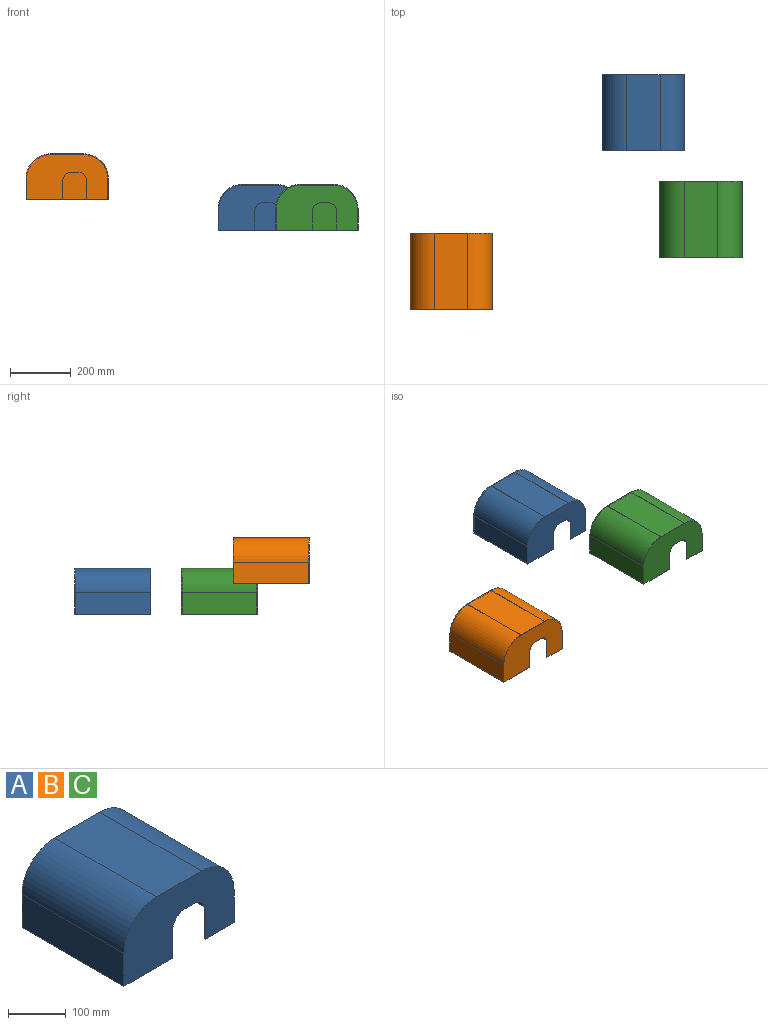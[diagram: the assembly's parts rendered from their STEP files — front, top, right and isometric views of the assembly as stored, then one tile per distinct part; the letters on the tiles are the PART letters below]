
ASSEMBLY  parts=3 mates=2
PART A: 26 faces, bbox 270x250x150 mm
  f0: plane 250x120mm, normal (0,0,-1), area 987.5mm2, adj f1,f4,f6,f10,f12,f13,f20,f21
  f1: plane 270x150mm, normal (0,1,0), area 30939.4mm2, adj f0,f2,f3,f4,f5,f7,f8,f21
  f2: plane 250x160mm, normal (0,0,-1), area 1187.5mm2, adj f1,f5,f6,f11,f12,f13,f16,f25
  f3: plane 250x110mm, normal (0,0,1), area 27500mm2, adj f1,f6,f7,f8
  f4: plane 250x70mm, normal (-1,0,0), area 17500mm2, adj f0,f1,f6,f7
  f5: plane 250x70mm, normal (1,0,0), area 17500mm2, adj f1,f2,f6,f8
  f6: plane 270x150mm, normal (0,-1,0), area 30939.4mm2, adj f0,f2,f3,f4,f5,f7,f8,f16
  f7: cylinder r=80mm len=250mm, axis (0,1,0), area 31415.9mm2, adj f1,f3,f4,f6
  f8: cylinder r=80mm len=250mm, axis (0,-1,0), area 31415.9mm2, adj f1,f3,f5,f6
  f9: plane 245x110mm, normal (0,0,-1), area 26950mm2, adj f12,f13,f14,f15
  f10: plane 245x70mm, normal (1,0,0), area 17150mm2, adj f0,f12,f13,f14
  f11: plane 245x70mm, normal (-1,0,0), area 17150mm2, adj f2,f12,f13,f15
  f12: plane 265x147.5mm, normal (0,1,0), area 29695.9mm2, adj f0,f2,f9,f10,f11,f14,f15,f16
  f13: plane 265x147.5mm, normal (0,-1,0), area 29695.9mm2, adj f0,f2,f9,f10,f11,f14,f15,f21
  f14: cylinder r=77.5mm len=245mm, axis (0,1,0), area 29825.5mm2, adj f9,f10,f12,f13
  f15: cylinder r=77.5mm len=245mm, axis (0,-1,0), area 29825.5mm2, adj f9,f11,f12,f13
  f16: plane 60x2.5mm, normal (-1,0,0), area 150mm2, adj f2,f6,f12,f17
  f17: cylinder r=30mm len=30mm, axis (0,-1,0), area 117.8mm2, adj f6,f12,f16,f18
  f18: plane 20x2.5mm, normal (0,0,-1), area 50mm2, adj f6,f12,f17,f19
  f19: cylinder r=30mm len=30mm, axis (0,-1,0), area 117.8mm2, adj f6,f12,f18,f20
  f20: plane 60x2.5mm, normal (1,0,0), area 150mm2, adj f0,f6,f12,f19
  f21: plane 60x2.5mm, normal (1,0,0), area 150mm2, adj f0,f1,f13,f22
  f22: cylinder r=30mm len=30mm, axis (0,1,0), area 117.8mm2, adj f1,f13,f21,f23
  f23: plane 20x2.5mm, normal (0,0,-1), area 50mm2, adj f1,f13,f22,f24
  f24: cylinder r=30mm len=30mm, axis (0,1,0), area 117.8mm2, adj f1,f13,f23,f25
  f25: plane 60x2.5mm, normal (-1,0,0), area 150mm2, adj f1,f2,f13,f24
PART B: same geometry as A
PART C: same geometry as A
PLACE A t=(360.62,453.74,34.52)mm
PLACE B t=(-269.38,-65.87,134.49)mm
PLACE C t=(549.46,103.74,34.52)mm
MATE planar A.f6 <-> C.f8  axis (0,-1,0) through (305.62,203.74,184.52)mm
MATE planar A.f3 <-> C.f3  axis (0,0,1) through (415.62,328.74,184.52)mm
